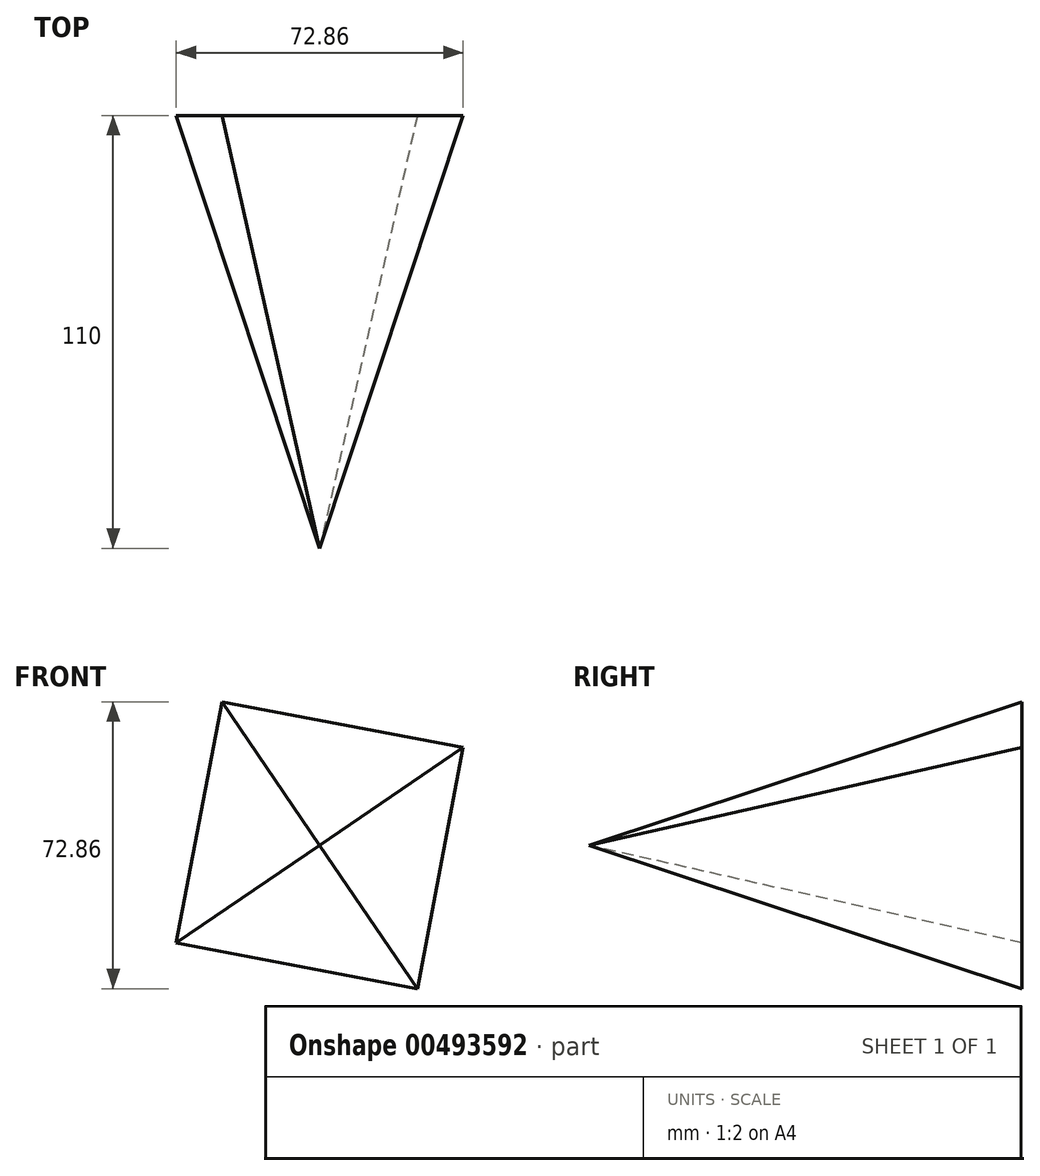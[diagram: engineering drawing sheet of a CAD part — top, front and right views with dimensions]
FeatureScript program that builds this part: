
annotation { "Feature Type Name" : "Feature", "Feature Type Description" : "" }
export const myFeature = defineFeature(function(context is Context, id is Id, definition is map)
    precondition{}
    {
        {
            var Q0;
            Q0=qCreatedBy(makeId("Front.planeOp"),FACE);
            var sketch = newSketch(context, id + "F0", { "sketchPlane" : qUnion([Q0])});
            skCircle(sketch, "E0.cCircle", {"center": v(0, 0) * mm, "radius": 44.08 * mm, "construction": true});
            skLineSegment(sketch, "E0.0", {"start": v(-36.43, -24.82) * mm, "end": v(-24.82, 36.43) * mm});
            skLineSegment(sketch, "E0.1", {"start": v(-24.82, 36.43) * mm, "end": v(36.43, 24.82) * mm});
            skLineSegment(sketch, "E0.2", {"start": v(36.43, 24.82) * mm, "end": v(24.82, -36.43) * mm});
            skLineSegment(sketch, "E0.3", {"start": v(24.82, -36.43) * mm, "end": v(-36.43, -24.82) * mm});
            skSolve(sketch);
        }
        {
            var Q0;
            Q0=qCreatedBy(makeId("Front.planeOp"),FACE);
            cPlane(context, id + "F1", {"entities" : qUnion([Q0]), "cplaneType" : CPlaneType.OFFSET, "offset" : 110 * mm, "width" : 150 * mm, "height" : 150 * mm});
        }
        {
            var Q0;
            Q0=qCreatedBy(id+"F1.planeOp",FACE);
            var sketch = newSketch(context, id + "F2", { "sketchPlane" : qUnion([Q0])});
            skPoint(sketch, "E1", {"position": v(0, 0) * mm});
            skSolve(sketch);
        }
        {
            var Q0;
            Q0=makeQuery(id+"F0.imprint","IMPRINT",FACE,{"disambiguationData":[TD([[makeQuery(id+"F0.imprint","IMPRINT",EDGE,{"derivedFrom":sQuery(id+"F0.wireOp",EDGE,"E0.0")}),-1.0]])]});
            var Q1;
            Q1=sQuery(id+"F2.wireOp",VERTEX,"E1");
            loft(context, id + "F3", {"sheetProfilesArray" : [{ "sheetProfileEntities" : qUnion([Q0]) }, { "sheetProfileEntities" : qUnion([Q1]) }]});
        }
    });
